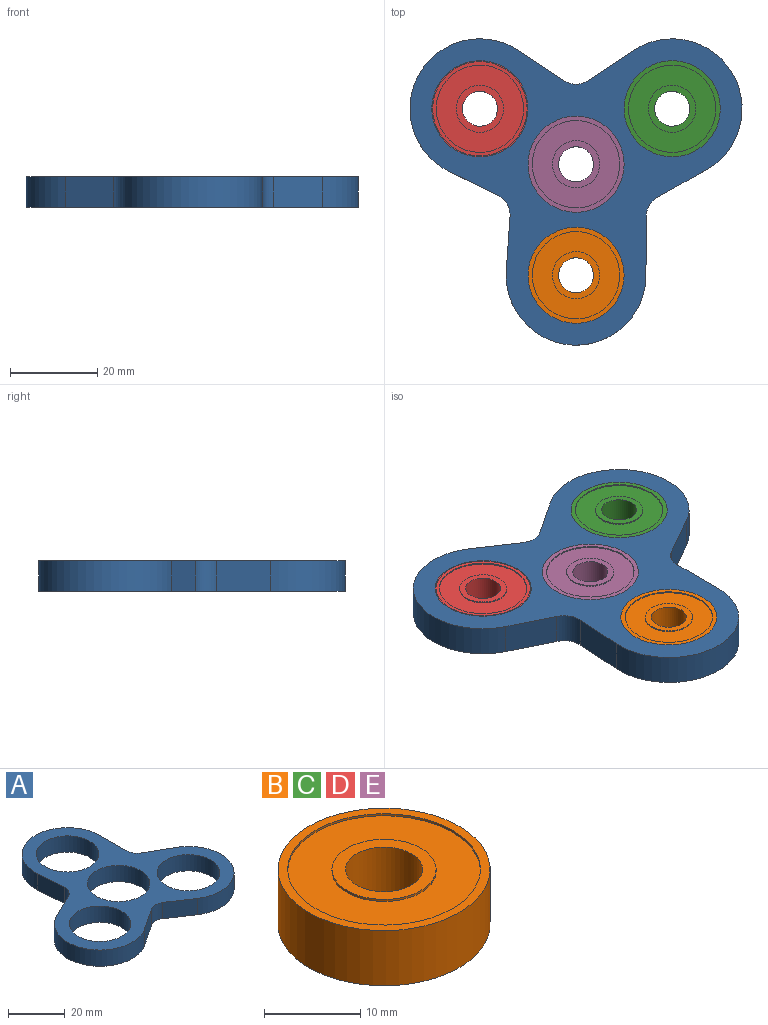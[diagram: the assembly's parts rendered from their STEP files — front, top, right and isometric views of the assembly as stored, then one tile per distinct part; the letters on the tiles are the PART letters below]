
ASSEMBLY  parts=5 mates=4
PART A: 18 faces, bbox 76x70.1x7 mm
  f0: cylinder r=16mm len=29.95mm, axis (0,0,-1), area 360.3mm2, adj f1,f12,f13,f14
  f1: plane 11.2x7mm, normal (0.49,0.87,0), area 89.9mm2, adj f0,f13,f14,f15
  f2: plane 13.49x7mm, normal (1,0,0), area 94.4mm2, adj f3,f13,f14,f15
  f3: cylinder r=16mm len=32mm, axis (0,0,-1), area 359.4mm2, adj f2,f4,f13,f14
  f4: plane 12.28x7mm, normal (-1,-0.07,0), area 86.2mm2, adj f3,f13,f14,f16
  f5: plane 11.07x7mm, normal (-0.44,0.9,0), area 86.2mm2, adj f6,f13,f14,f16
  f6: cylinder r=16mm len=30.38mm, axis (0,0,-1), area 366.9mm2, adj f5,f7,f13,f14
  f7: plane 10.32x7mm, normal (0.55,-0.83,0), area 86.7mm2, adj f6,f13,f14,f17
  f8: cylinder r=11mm len=22mm, axis (0,0,-1), area 483.8mm2, adj f13,f14
  f9: cylinder r=11mm len=22mm, axis (0,0,-1), area 483.8mm2, adj f13,f14
  f10: cylinder r=10.79mm len=21.59mm, axis (0,0,-1), area 474.8mm2, adj f13,f14
  f11: cylinder r=11mm len=22mm, axis (0,0,-1), area 483.8mm2, adj f13,f14
  f12: plane 10.32x7mm, normal (-0.55,-0.83,0), area 86.7mm2, adj f0,f13,f14,f17
  f13: plane 75.99x70.1mm, normal (0,0,1), area 1665.2mm2, adj f0,f1,f2,f3,f4,f5,f6,f7
  f14: plane 75.99x70.1mm, normal (0,0,-1), area 1665.2mm2, adj f0,f1,f2,f3,f4,f5,f6,f7
  f15: cylinder r=5.08mm len=7mm, axis (0,0,-1), area 37.6mm2, adj f1,f2,f13,f14
  f16: cylinder r=5.08mm len=7mm, axis (0,0,-1), area 42.2mm2, adj f4,f5,f13,f14
  f17: cylinder r=5.08mm len=7mm, axis (0,0,-1), area 41.8mm2, adj f7,f12,f13,f14
PART B: 12 faces, bbox 22x22x7 mm
  f0: plane 10.8x10.8mm, normal (0,0,-1), area 41.3mm2, adj f5,f11
  f1: plane 10.8x10.8mm, normal (0,0,1), area 41.3mm2, adj f5,f8
  f2: plane 22x22mm, normal (0,0,1), area 66.3mm2, adj f4,f6
  f3: plane 22x22mm, normal (0,0,-1), area 66.3mm2, adj f4,f10
  f4: cylinder r=11mm len=22mm, axis (0,0,-1), area 483.8mm2, adj f2,f3
  f5: cylinder r=4mm len=8mm, axis (0,0,-1), area 175.9mm2, adj f0,f1
  f6: cylinder r=9.99mm len=19.99mm, axis (0,0,1), area 16mm2, adj f2,f7
  f7: plane 19.99x19.99mm, normal (0,0,1), area 222.2mm2, adj f6,f8
  f8: cylinder r=5.4mm len=10.8mm, axis (0,0,1), area 8.6mm2, adj f1,f7
  f9: plane 19.99x19.99mm, normal (0,0,-1), area 222.2mm2, adj f10,f11
  f10: cylinder r=9.99mm len=19.99mm, axis (0,0,-1), area 16mm2, adj f3,f9
  f11: cylinder r=5.4mm len=10.8mm, axis (0,0,-1), area 8.6mm2, adj f0,f9
PART C: same geometry as B
PART D: same geometry as B
PART E: same geometry as B
PLACE A rot(axis=(1,0,0),180deg) t=(-8.67,-32.94,32.43)mm
PLACE B t=(-8.67,-58.34,28.93)mm
PLACE C t=(13.33,-20.24,28.93)mm
PLACE D t=(-30.67,-20.24,28.93)mm
PLACE E t=(-8.67,-32.94,28.93)mm
MATE fastened A.f6 <-> D.f4  axis (0,0,1) through (-30.67,-20.24,32.43)mm
MATE fastened A.f0 <-> C.f4  axis (0,0,1) through (13.33,-20.24,25.43)mm
MATE fastened A.f3 <-> B.f4  axis (0,0,1) through (-8.67,-58.34,25.43)mm
MATE fastened A.f9 <-> E.f4  axis (0,0,1) through (-8.67,-32.94,32.43)mm
